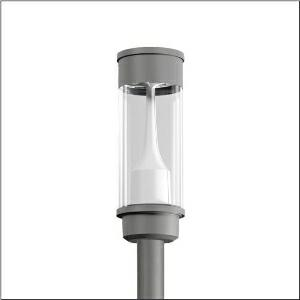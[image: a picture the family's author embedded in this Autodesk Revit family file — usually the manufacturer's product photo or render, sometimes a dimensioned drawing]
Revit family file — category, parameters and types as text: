
# Revit family: litepole_iq___p1_0a_5xa5415bf14h_51c2
name_source: partatom
category: Lighting Fixtures
units: mm (PartAtom-declared; Revit-internal decimal feet)

## family parameters
Cut with Voids When Loaded = No
Host = Face
Light Source = No
Part Type = Normal
Room Calculation Point = No
Round Connector Dimension = Use Diameter
Shared = No

## types (1)
- --- (1 x LED, 1510 lm, 12.9 W, 2200K)
    Apparent Load = 13 VA
    CIE Flux Codes = 32 61 90 93 100
    Color Rendering = 70
    Color Temperature = 2200K
    Default Elevation = 1800 mm
    Description = Litepole iQ, mast luminaire, Module 540 iQ-SR, primary light control with 3 zone facetted reflector, of plastic, silver coated, highly specular, structured, primary optical cover: cover, of PMMA, transparent, partly coated, light distribution: P1.0a, light emission: direct distribution, primary light characteristic: strongly asymmetric, installation type: post-top, LED, High Power LED, rated luminous flux: 1.510lm, luminous efficacy: 117lm/W, light colour: 722, colour temperature: 2200K, control gear: ECG iQ, control: optimised constant luminous flux control (CLO 2.0), Desk-Remote (wireless, voltage-free reading and setting of iQ features in the workshop via application-optimized NFC function/RFID function), Light-Fading, Smart-Wire, Night-Set, Lumen-Switch, Temp-Guard, Auto-Match, Street-Remote, presetting dimming logarithmic, with terminal, 6-pole, max. 2.5mm², mains connection: 220..240V, AC, 50/60Hz, start of lifetime: 13W, end of lifetime: 13W, reduction: 6W, luminaire housing, upper part, of glass-fibre reinforced polyester, coated, Siteco® metallic grey (DB 702S), diameter: 210mm, height: 590mm, spigot size: d x l = 76 x 70mm (post-top) | with reducer (optional accessory) 60 x 70mm, post-top mast mounting element, of diecast aluminium, coated, Siteco® metallic grey (DB 702S), Module 540 iQ-SR, traffic white (RAL 9016), equipment: standard, protection rating (complete): IP65, insulation class (complete): insulation class II (safety insulation), certification: CE, ENEC, VDE, packaging unit: 1 piece

Light Distribution: P1.0a
    Height = 590 mm
    Lamp = 1 x LED
    Lamp Light Flux = 1510 lm
    Lamp Power = 12.9 W
    Lamp count = 1
    Length = 220 mm
    Luminous efficacy = 117 lm/W
    Manufacturer = Siteco
    ModVariant = No
    Model = 5XA5415BF14H
    Number of Poles = 1
    OnlyDefault = Yes
    Power Factor = 1
    Product Name = Litepole iQ | P1.0a
    Product group = mast luminaire | pylon top
    ProductGroupID = 6100
    Protection Class = Protection class II
    Protection Degree = IP 65
    RLX_Detail_Level = 1
    RlxData = <blob elided: 64333 chars, md5=daf272c9>
    Socket = socket
    Standby Power = 0 W
    System Light Flux = 1510 lm
    System Power = 13 W
    Type Comments = factory setting: luminous flux: 100 % | dim-lin: 254 | 516 mA
    Type Image = l_1006025.jpg
    URL = http://relux.com
    VarID = @adj_070007
    Voltage = 0 V
    Weight = 0.00 kg
    Width = 0 mm  [stored 0 ft]

note: [stored X ft] marks values corroborated as IEEE doubles in the binary element streams (Revit-internal decimal feet)

## geometry (parser evidence)
native form markers: Blend x4, Sweep x14
no freeform markers — native parametric forms only
